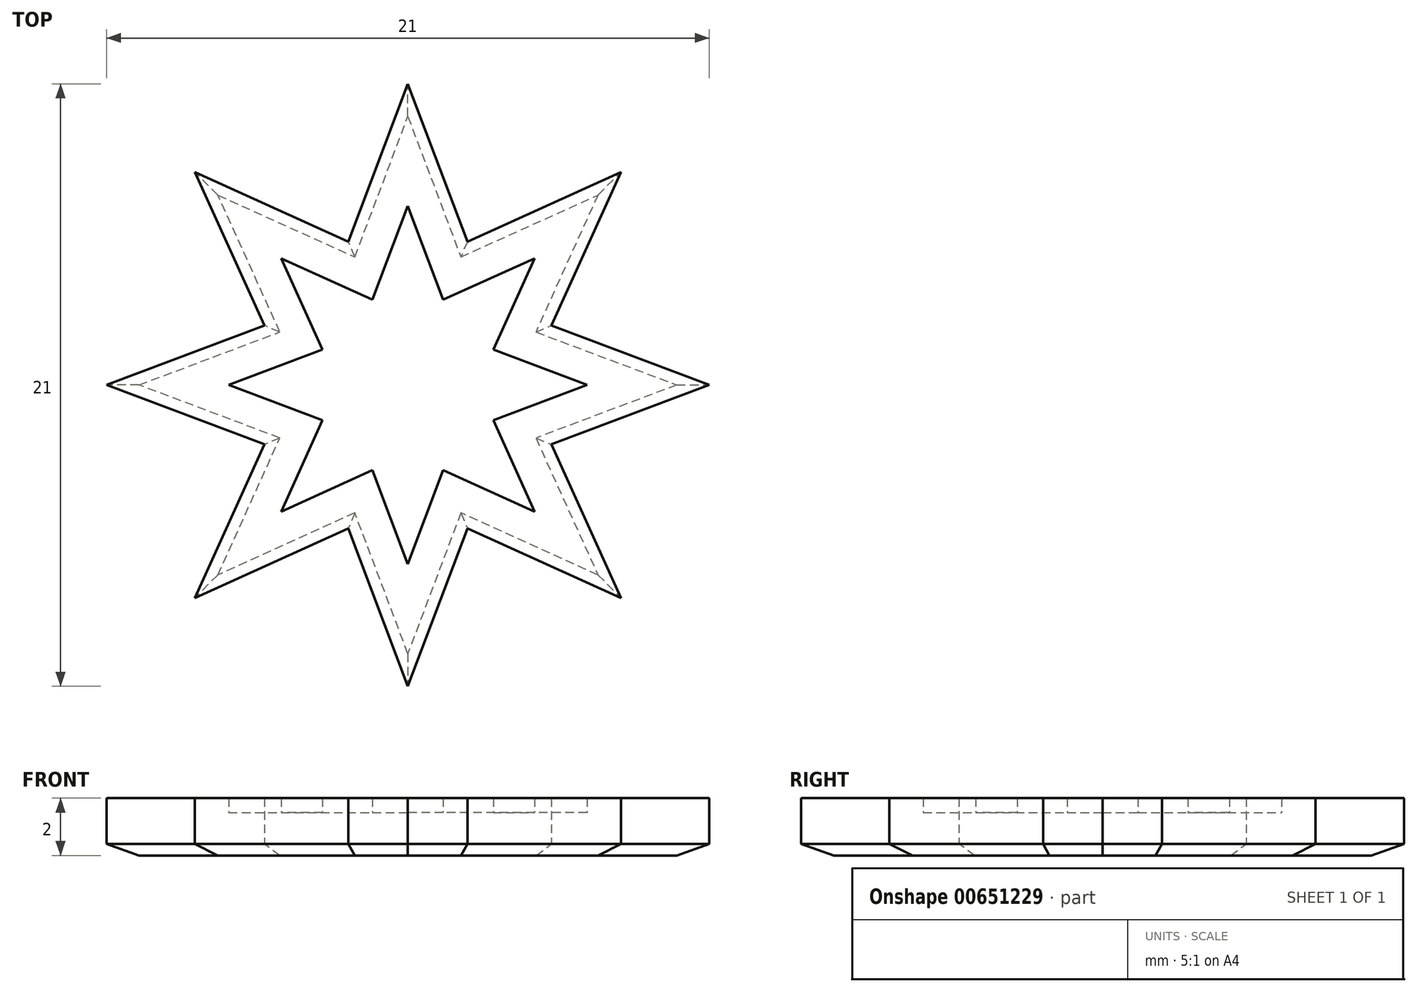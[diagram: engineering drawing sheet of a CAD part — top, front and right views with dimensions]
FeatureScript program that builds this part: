
annotation { "Feature Type Name" : "Feature", "Feature Type Description" : "" }
export const myFeature = defineFeature(function(context is Context, id is Id, definition is map)
    precondition{}
    {
        {
            var Q0;
            Q0=qCreatedBy(makeId("Top.planeOp"),FACE);
            var sketch = newSketch(context, id + "F0", { "sketchPlane" : qUnion([Q0])});
            skLineSegment(sketch, "E0.bottom", {"start": v(12.5, 12.5) * mm, "end": v(-12.5, 12.5) * mm});
            skLineSegment(sketch, "E0.top", {"start": v(12.5, -12.5) * mm, "end": v(-12.5, -12.5) * mm});
            skLineSegment(sketch, "E0.left", {"start": v(12.5, 12.5) * mm, "end": v(12.5, -12.5) * mm});
            skLineSegment(sketch, "E0.right", {"start": v(-12.5, 12.5) * mm, "end": v(-12.5, -12.5) * mm});
            skPoint(sketch, "E0.middle", {"position": v(0, 0) * mm});
            skCircle(sketch, "E1.cCircle", {"center": v(0, 0) * mm, "radius": 5 * mm, "construction": true});
            skLineSegment(sketch, "E1.6", {"start": v(-2.07, 5) * mm, "end": v(2.07, 5) * mm, "construction": true});
            skPoint(sketch, "E1.0.midPoint", {"position": v(5, 0) * mm});
            skLineSegment(sketch, "E2", {"start": v(-2.07, 5) * mm, "end": v(0, 10.5) * mm});
            skLineSegment(sketch, "E3", {"start": v(0, 10.5) * mm, "end": v(2.07, 5) * mm});
            skPoint(sketch, "E4.endSnap0", {"position": v(0, -8.67) * mm});
            skLineSegment(sketch, "E5", {"start": v(-2.07, 5) * mm, "end": v(0, 0) * mm, "construction": true});
            skLineSegment(sketch, "E6", {"start": v(2.07, 5) * mm, "end": v(0, 0) * mm, "construction": true});
            skPoint(sketch, "E7", {"position": v(0, 12.5) * mm});
            skLineSegment(sketch, "E8.1.0", {"start": v(-7.42, 7.42) * mm, "end": v(-2.07, 5) * mm});
            skLineSegment(sketch, "E8.1.1", {"start": v(-5, 2.07) * mm, "end": v(-7.42, 7.42) * mm});
            skLineSegment(sketch, "E8.2.0", {"start": v(-10.5, 0) * mm, "end": v(-5, 2.07) * mm});
            skLineSegment(sketch, "E8.2.1", {"start": v(-5, -2.07) * mm, "end": v(-10.5, 0) * mm});
            skLineSegment(sketch, "E8.3.0", {"start": v(-7.42, -7.42) * mm, "end": v(-5, -2.07) * mm});
            skLineSegment(sketch, "E8.3.1", {"start": v(-2.07, -5) * mm, "end": v(-7.42, -7.42) * mm});
            skLineSegment(sketch, "E8.4.0", {"start": v(0, -10.5) * mm, "end": v(-2.07, -5) * mm});
            skLineSegment(sketch, "E8.4.1", {"start": v(2.07, -5) * mm, "end": v(0, -10.5) * mm});
            skLineSegment(sketch, "E8.5.0", {"start": v(7.42, -7.42) * mm, "end": v(2.07, -5) * mm});
            skLineSegment(sketch, "E8.5.1", {"start": v(5, -2.07) * mm, "end": v(7.42, -7.42) * mm});
            skLineSegment(sketch, "E8.6.0", {"start": v(10.5, 0) * mm, "end": v(5, -2.07) * mm});
            skLineSegment(sketch, "E8.6.1", {"start": v(5, 2.07) * mm, "end": v(10.5, 0) * mm});
            skLineSegment(sketch, "E8.7.0", {"start": v(7.42, 7.42) * mm, "end": v(5, 2.07) * mm});
            skLineSegment(sketch, "E8.7.1", {"start": v(2.07, 5) * mm, "end": v(7.42, 7.42) * mm});
            skSolve(sketch);
        }
        {
            var Q0;
            Q0=makeQuery(id+"F0.imprint","IMPRINT",FACE,{"disambiguationData":[TD([[makeQuery(id+"F0.imprint","IMPRINT",EDGE,{"derivedFrom":sQuery(id+"F0.wireOp",EDGE,"E2")}),-1.0]])]});
            extrude(context, id + "F1", {"entities" : qUnion([Q0]), "depth" : 2 * mm, "offsetDistance" : 25 * mm});
        }
        {
            var Q0;
            Q0=makeQuery(id+"F1.opExtrude","CAP_FACE",FACE,{"disambiguationData":[OSD([sQuery(id+"F0.wireOp",EDGE,"E2"),sQuery(id+"F0.wireOp",EDGE,"E3"),sQuery(id+"F0.wireOp",EDGE,"E8.1.0"),sQuery(id+"F0.wireOp",EDGE,"E8.1.1"),sQuery(id+"F0.wireOp",EDGE,"E8.2.0"),sQuery(id+"F0.wireOp",EDGE,"E8.2.1"),sQuery(id+"F0.wireOp",EDGE,"E8.3.0"),sQuery(id+"F0.wireOp",EDGE,"E8.3.1"),sQuery(id+"F0.wireOp",EDGE,"E8.4.0"),sQuery(id+"F0.wireOp",EDGE,"E8.4.1"),sQuery(id+"F0.wireOp",EDGE,"E8.5.0"),sQuery(id+"F0.wireOp",EDGE,"E8.5.1"),sQuery(id+"F0.wireOp",EDGE,"E8.6.0"),sQuery(id+"F0.wireOp",EDGE,"E8.6.1"),sQuery(id+"F0.wireOp",EDGE,"E8.7.0"),sQuery(id+"F0.wireOp",EDGE,"E8.7.1")])],"isStart":false});
            shell(context, id + "F2", {"entities" : qUnion([Q0]), "thickness" : 1.5 * mm});
        }
        {
            var Q0;
            Q0=makeQuery(id+"F1.opExtrude","CAP_FACE",FACE,{"disambiguationData":[OSD([sQuery(id+"F0.wireOp",EDGE,"E2"),sQuery(id+"F0.wireOp",EDGE,"E3"),sQuery(id+"F0.wireOp",EDGE,"E8.1.0"),sQuery(id+"F0.wireOp",EDGE,"E8.1.1"),sQuery(id+"F0.wireOp",EDGE,"E8.2.0"),sQuery(id+"F0.wireOp",EDGE,"E8.2.1"),sQuery(id+"F0.wireOp",EDGE,"E8.3.0"),sQuery(id+"F0.wireOp",EDGE,"E8.3.1"),sQuery(id+"F0.wireOp",EDGE,"E8.4.0"),sQuery(id+"F0.wireOp",EDGE,"E8.4.1"),sQuery(id+"F0.wireOp",EDGE,"E8.5.0"),sQuery(id+"F0.wireOp",EDGE,"E8.5.1"),sQuery(id+"F0.wireOp",EDGE,"E8.6.0"),sQuery(id+"F0.wireOp",EDGE,"E8.6.1"),sQuery(id+"F0.wireOp",EDGE,"E8.7.0"),sQuery(id+"F0.wireOp",EDGE,"E8.7.1")])],"isStart":true});
            chamfer(context, id + "F3", {"entities" : qUnion([Q0]), "width" : .4 * mm, "tangentPropagation" : true});
        }
    });
